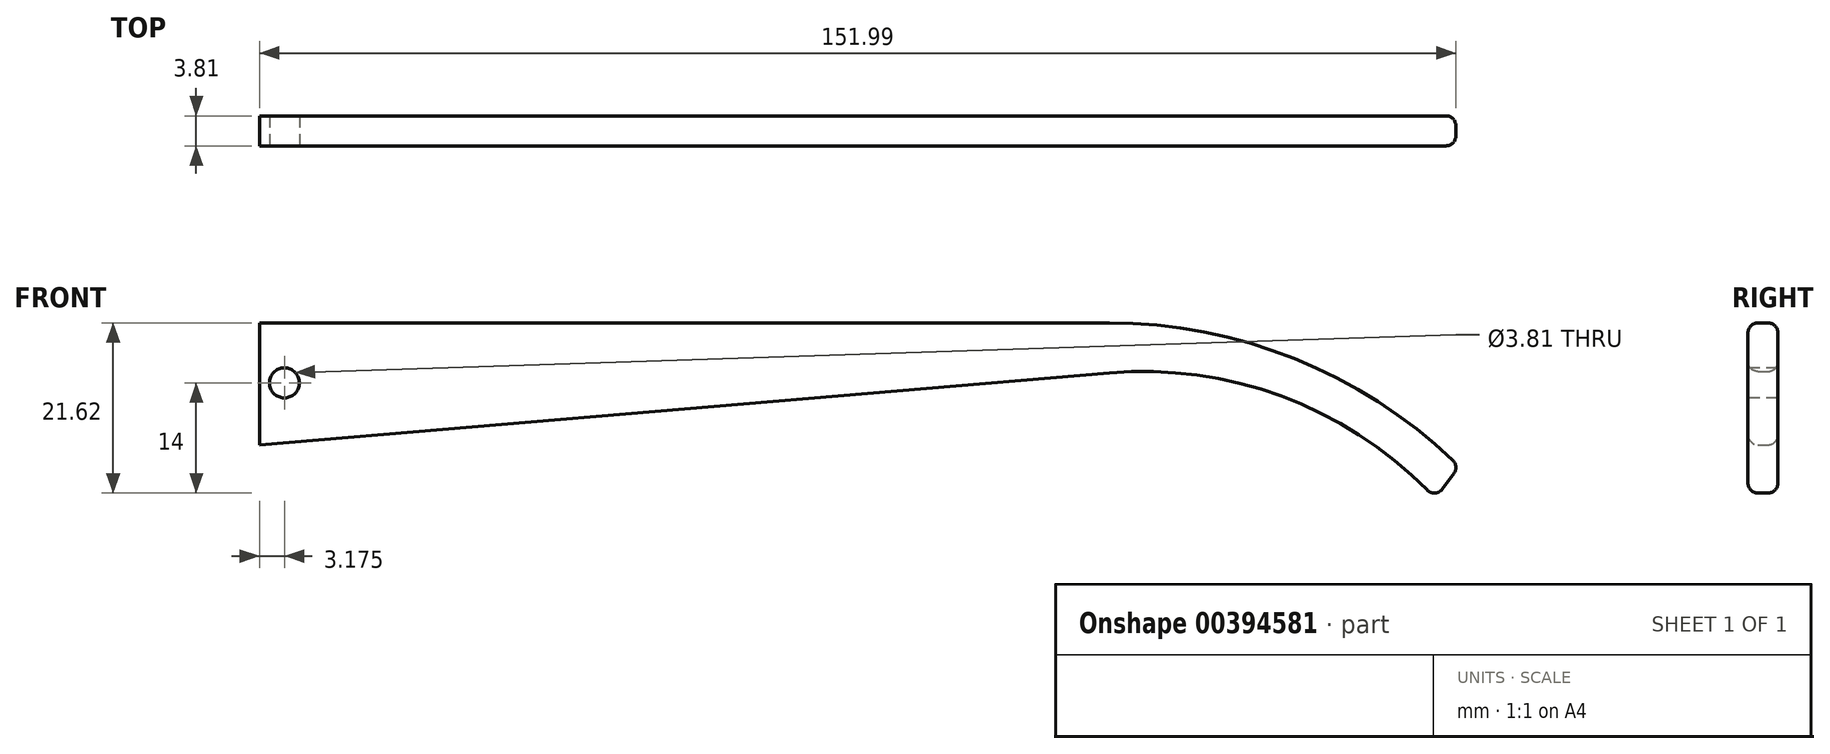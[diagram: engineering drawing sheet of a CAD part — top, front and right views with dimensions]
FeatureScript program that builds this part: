
annotation { "Feature Type Name" : "Feature", "Feature Type Description" : "" }
export const myFeature = defineFeature(function(context is Context, id is Id, definition is map)
    precondition{}
    {
        {
            var Q0;
            Q0=qCreatedBy(makeId("Front.planeOp"),FACE);
            var sketch = newSketch(context, id + "F0", { "sketchPlane" : qUnion([Q0])});
            skLineSegment(sketch, "E0", {"start": v(-107.95, 6.35) * mm, "end": v(0, 6.35) * mm});
            skArc(sketch, "E1", {"start": v(44.45, -11.88) * mm, "mid": v(24.02, 1.62) * mm, "end": v(0, 6.35) * mm});
            skLineSegment(sketch, "E2", {"start": v(-107.95, 6.35) * mm, "end": v(-107.95, -9.14) * mm});
            skLineSegment(sketch, "E3", {"start": v(-107.95, -9.14) * mm, "end": v(0, 0) * mm});
            skArc(sketch, "E4", {"start": v(41.43, -15.96) * mm, "mid": v(22.55, -3.21) * mm, "end": v(0, 0) * mm});
            skLineSegment(sketch, "E5", {"start": v(44.45, -11.88) * mm, "end": v(41.43, -15.96) * mm});
            skSolve(sketch);
        }
        {
            var Q0;
            Q0=makeQuery(id+"F0.imprint","IMPRINT",FACE,{"disambiguationData":[TD([[makeQuery(id+"F0.imprint","IMPRINT",EDGE,{"derivedFrom":sQuery(id+"F0.wireOp",EDGE,"E0")}),-1.0]])]});
            extrude(context, id + "F1", {"entities" : qUnion([Q0]), "depth" : 3.8 * mm});
        }
        {
            var Q0;
            Q0=makeQuery(id+"F1.opExtrude","CAP_FACE",FACE,{"disambiguationData":[OSD([sQuery(id+"F0.wireOp",EDGE,"E0"),sQuery(id+"F0.wireOp",EDGE,"E1"),sQuery(id+"F0.wireOp",EDGE,"E2"),sQuery(id+"F0.wireOp",EDGE,"E3"),sQuery(id+"F0.wireOp",EDGE,"E4"),sQuery(id+"F0.wireOp",EDGE,"E5")])],"isStart":false});
            var sketch = newSketch(context, id + "F2", { "sketchPlane" : qUnion([Q0])});
            skCircle(sketch, "E6", {"center": v(-104.78, -1.27) * mm, "radius": 1.9 * mm});
            skSolve(sketch);
        }
        {
            var Q0;
            Q0=makeQuery(id+"F2.imprint","IMPRINT",FACE,{"disambiguationData":[TD([[makeQuery(id+"F2.imprint","IMPRINT",EDGE,{"derivedFrom":sQuery(id+"F2.wireOp",EDGE,"E6")}),1.0]])]});
            extrude(context, id + "F3", {"entities" : qUnion([Q0]), "operationType" : NewBodyOperationType.REMOVE, "endBound" : BoundingType.THROUGH_ALL, "oppositeDirection" : true, "depth" : 25.4 * mm});
        }
        {
            var Q0;
            Q0=makeQuery(id+"F1.opExtrude","CAP_EDGE",EDGE,{"disambiguationData":[OSD([sQuery(id+"F0.wireOp",EDGE,"E0")])],"isStart":false});
            var Q1;
            Q1=makeQuery(id+"F1.opExtrude","CAP_EDGE",EDGE,{"disambiguationData":[OSD([sQuery(id+"F0.wireOp",EDGE,"E3")])],"isStart":false});
            var Q2;
            Q2=makeQuery(id+"F1.opExtrude","CAP_EDGE",EDGE,{"disambiguationData":[OSD([sQuery(id+"F0.wireOp",EDGE,"E0")])],"isStart":true});
            var Q3;
            Q3=makeQuery(id+"F1.opExtrude","CAP_EDGE",EDGE,{"disambiguationData":[OSD([sQuery(id+"F0.wireOp",EDGE,"E3")])],"isStart":true});
            fillet(context, id + "F4", {"entities" : qUnion([Q0, Q1, Q2, Q3]), "radius" : 1.27 * mm, "tangentPropagation" : true, "allowEdgeOverflow" : false});
        }
        {
            var Q0;
            Q0=makeQuery(id+"F1.opExtrude","CAP_EDGE",EDGE,{"disambiguationData":[OSD([sQuery(id+"F0.wireOp",EDGE,"E5")])],"isStart":false});
            fillet(context, id + "F5", {"entities" : qUnion([Q0]), "radius" : 1.27 * mm, "tangentPropagation" : true, "allowEdgeOverflow" : false});
        }
    });
